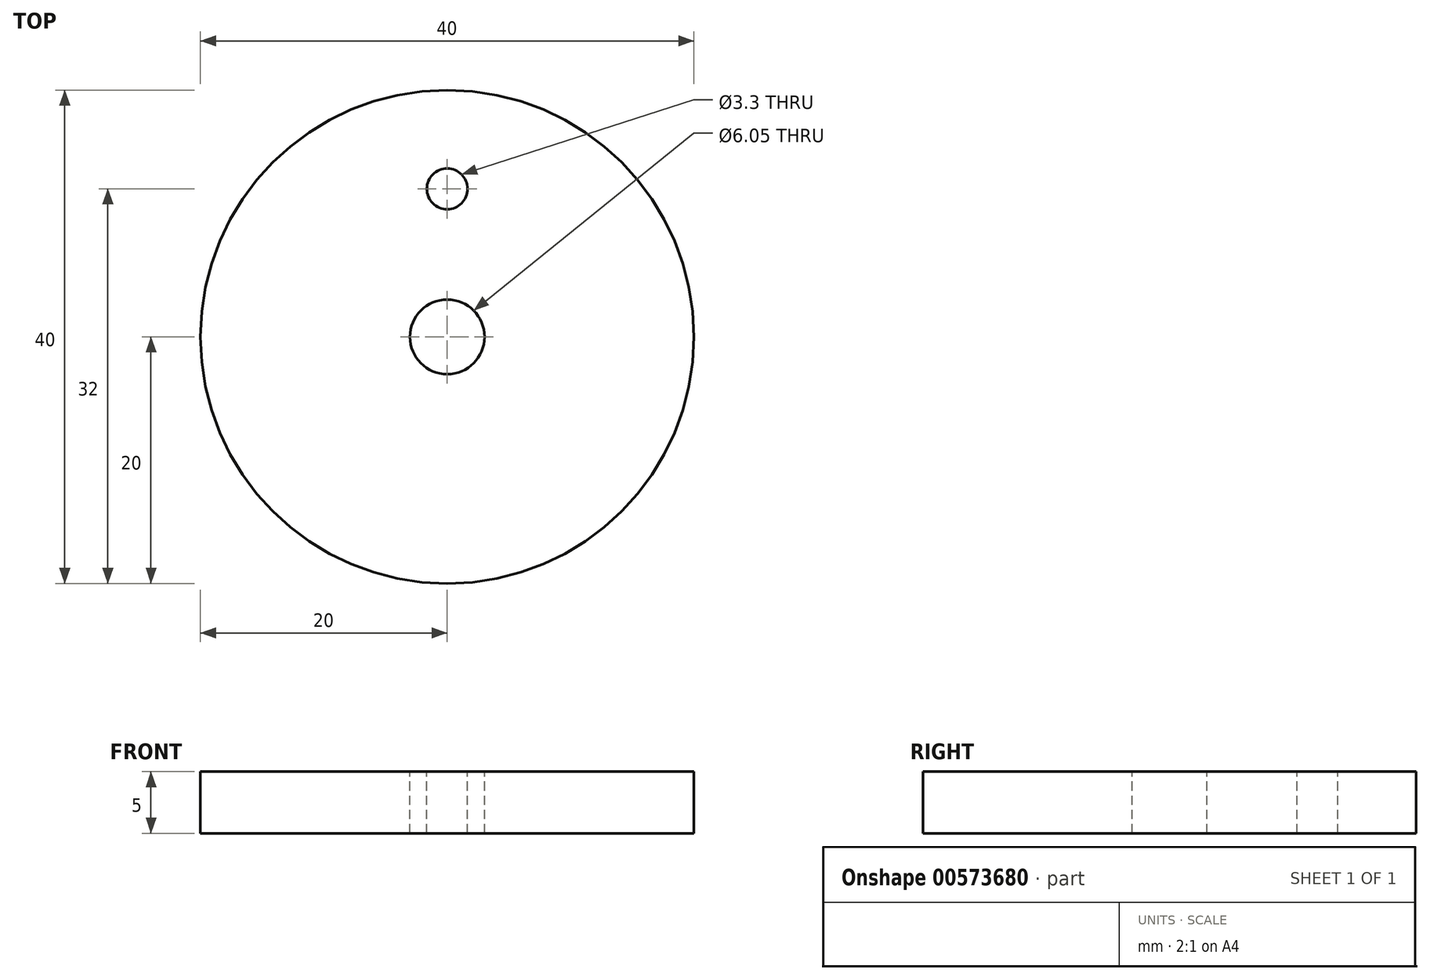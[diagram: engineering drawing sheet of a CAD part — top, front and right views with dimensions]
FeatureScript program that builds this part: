
annotation { "Feature Type Name" : "Feature", "Feature Type Description" : "" }
export const myFeature = defineFeature(function(context is Context, id is Id, definition is map)
    precondition{}
    {
        {
            var Q0;
            Q0=qCreatedBy(makeId("Top.planeOp"),FACE);
            var sketch = newSketch(context, id + "F0", { "sketchPlane" : qUnion([Q0])});
            skCircle(sketch, "E0", {"center": v(0, 0) * mm, "radius": 20 * mm});
            skSolve(sketch);
        }
        {
            var Q0;
            Q0=qSketchRegion(id+"F0",true);
            extrude(context, id + "F1", {"entities" : qUnion([Q0]), "depth" : 5 * mm, "offsetDistance" : 25.4 * mm});
        }
        {
            var Q0;
            Q0=makeQuery(id+"F1.opExtrude","CAP_FACE",FACE,{"disambiguationData":[OSD([sQuery(id+"F0.wireOp",EDGE,"E0")])],"isStart":false});
            var sketch = newSketch(context, id + "F2", { "sketchPlane" : qUnion([Q0])});
            skCircle(sketch, "E1", {"center": v(0, 0) * mm, "radius": 12 * mm});
            skPoint(sketch, "E2", {"position": v(0, 12) * mm});
            skSolve(sketch);
        }
        {
            var Q0;
            Q0=sQuery(id+"F2.wireOp",VERTEX,"E2");
            var Q1;
            Q1=makeQuery(id+"F1.opExtrude","SWEPT_BODY",BODY,{"disambiguationData":[OSD([sQuery(id+"F0.wireOp",EDGE,"E0")])]});
            hole(context, id + "F3", {"style" : HoleStyle.SIMPLE, "endStyle" : HoleEndStyle.THROUGH, "standardTappedOrClearance" : lookupTablePath({ "standard" : "ISO", "fit" : "Normal", "size" : "M3", "type" : "Clearance" }), "standardBlindInLast" : lookupTablePath({ "fit" : "Standard", "standard" : "ISO", "size" : "M3", "type" : "Clearance" }), "holeDiameter" : 3.3 * mm, "isTappedThrough" : true, "tappedDepth" : 12.7 * mm, "tapClearance" : 3, "locations" : qUnion([Q0]), "scope" : qUnion([Q1])});
        }
        {
            var Q0;
            Q0=makeQuery(id+"F1.opExtrude","CAP_FACE",FACE,{"disambiguationData":[OSD([sQuery(id+"F0.wireOp",EDGE,"E0")])],"isStart":false});
            var sketch = newSketch(context, id + "F4", { "sketchPlane" : qUnion([Q0])});
            skCircle(sketch, "E3", {"center": v(0, 0) * mm, "radius": 3.02 * mm});
            skSolve(sketch);
        }
        {
            var Q0;
            Q0=sQuery(id+"F4.wireOp",VERTEX,"E3.center");
            var Q1;
            Q1=makeQuery(id+"F1.opExtrude","SWEPT_BODY",BODY,{"disambiguationData":[OSD([sQuery(id+"F0.wireOp",EDGE,"E0")])]});
            hole(context, id + "F5", {"style" : HoleStyle.SIMPLE, "endStyle" : HoleEndStyle.THROUGH, "holeDiameter" : 6.05 * mm, "isTappedThrough" : true, "tappedDepth" : 12.7 * mm, "tapClearance" : 3, "locations" : qUnion([Q0]), "scope" : qUnion([Q1])});
        }
    });
